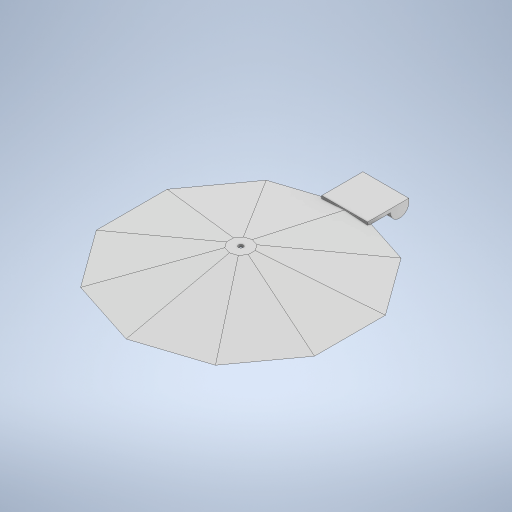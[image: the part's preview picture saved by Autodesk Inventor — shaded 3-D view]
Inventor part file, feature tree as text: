
AUTODESK INVENTOR PART (.ipt)
format: ipt  version: 2024 (Build 280153000, 153)  size: 318,464 bytes
history: native  units: mm
features: sketch x4, plane x1, loft x1, shell x1, extrude x1, hole x1
ambient origin geometry x8: Origin, YZ Plane, XZ Plane, XY Plane, X Axis, Y Axis, Z Axis, Center Point
bodies: Solid1 (feature_tree)
feature tree (9):
  sketch  "Sketch1"  dims[d0=100.0mm d1=29.389mm d2=10.0mm]
  plane  "Work Plane1"
  loft  "Loft1"
  shell  "Shell1"  Thickness=10.0mm
  extrude  "Extrusion2"  Depth=10.0mm
  hole  "Hole1"  [1 undecoded]
  sketch  "Sketch2"  dims[d3=10.0mm d4=2.939mm]
  sketch  "Sketch4"  dims[d5=0.0mm d6=90.0deg d7=0.0mm d8=90.0deg]
  sketch  "Sketch6"  dims[d9=1.0mm d18=1.5mm d21=4.0mm d22=18.0mm d23=20.0mm d24=0.0mm d28=2.0mm d29=6.0mm d30=4.0mm d31=2.0mm d32=90.0deg d33=8.0mm d34=20.594885mm d35=0.75mm d36=20.594885mm d37=0.0625mm d38=0.75mm d39=0.375mm]
note: 1 required parameter value undecoded (feature->parameter linkage not recoverable at this tier; creation-order binding heuristic only, values carry confidence <= 0.55)
